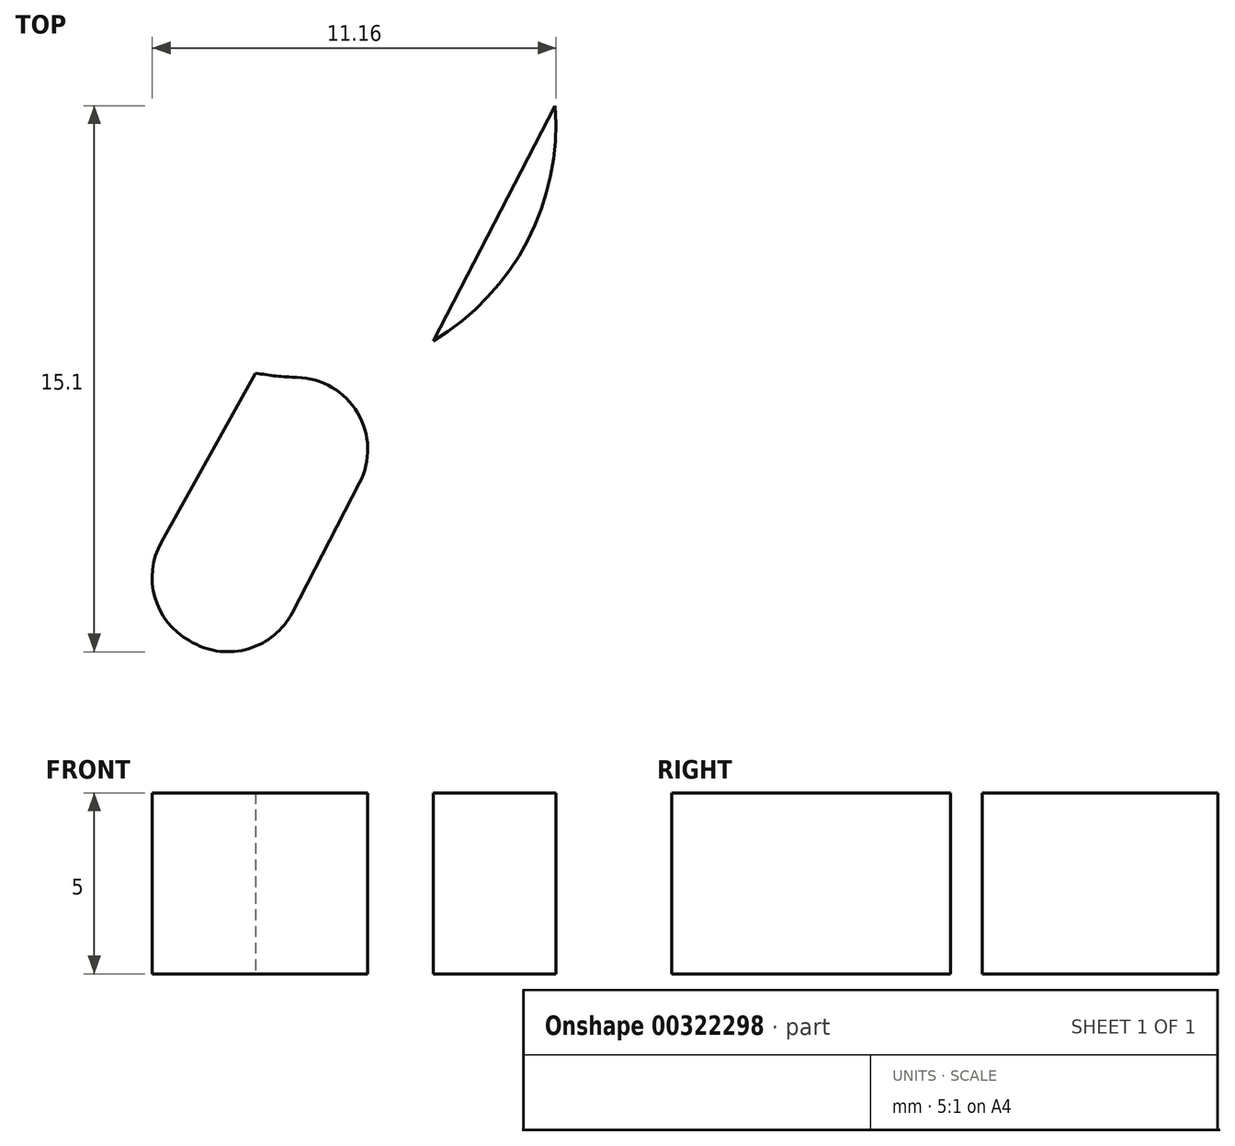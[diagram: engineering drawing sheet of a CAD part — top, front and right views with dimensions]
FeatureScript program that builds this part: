
annotation { "Feature Type Name" : "Feature", "Feature Type Description" : "" }
export const myFeature = defineFeature(function(context is Context, id is Id, definition is map)
    precondition{}
    {
        {
            var Q0;
            Q0=qCreatedBy(makeId("Top.planeOp"),FACE);
            var sketch = newSketch(context, id + "F0", { "sketchPlane" : qUnion([Q0])});
            skCircle(sketch, "E0", {"center": v(0, 0) * mm, "radius": 10 * mm, "construction": true});
            skArc(sketch, "E1", {"start": v(-8.14, 12.6) * mm, "mid": v(7.17, 13.17) * mm, "end": v(15, 0) * mm});
            skArc(sketch, "E2.0", {"start": v(-14.53, 20.34) * mm, "mid": v(14.2, 20.58) * mm, "end": v(24.18, -6.35) * mm});
            skLineSegment(sketch, "E3", {"start": v(15, 0) * mm, "end": v(15, 0) * mm});
            skLineSegment(sketch, "E4", {"start": v(-8.14, 12.6) * mm, "end": v(-14.53, 20.34) * mm});
            skLineSegment(sketch, "E5", {"start": v(15, 0) * mm, "end": v(-4.3, -37.44) * mm});
            skLineSegment(sketch, "E6", {"start": v(-1.24, -55.34) * mm, "end": v(24.18, -6.35) * mm});
            skLineSegment(sketch, "E7", {"start": v(0, -40) * mm, "end": v(17.35, -6.35) * mm, "construction": true});
            skCircle(sketch, "E8", {"center": v(13.03, -14.72) * mm, "radius": 0.5 * mm});
            skCircle(sketch, "E9", {"center": v(15.86, -9.24) * mm, "radius": 0.5 * mm});
            skCircle(sketch, "E10", {"center": v(4.12, -32) * mm, "radius": 0.5 * mm});
            skLineSegment(sketch, "E11", {"start": v(24.18, -6.35) * mm, "end": v(15, 0) * mm, "construction": true});
            skCircle(sketch, "E12", {"center": v(0, -40) * mm, "radius": 1.25 * mm});
            skLineSegment(sketch, "E13", {"start": v(-1.24, -55.34) * mm, "end": v(-4.88, -53.3) * mm});
            skLineSegment(sketch, "E14", {"start": v(-4.88, -53.3) * mm, "end": v(-0.98, -46.3) * mm});
            skCircle(sketch, "E15", {"center": v(0, -40) * mm, "radius": 3.5 * mm, "construction": true});
            skArc(sketch, "E16", {"start": v(-2.2, -33.35) * mm, "mid": v(-3.9, -45.82) * mm, "end": v(6.98, -39.5) * mm});
            skCircle(sketch, "E17", {"center": v(0, -40) * mm, "radius": 7.5 * mm, "construction": true});
            skSolve(sketch);
        }
        {
            var Q0;
            Q0=makeQuery(id+"F0.imprint","IMPRINT",FACE,{"disambiguationData":[TD([[makeQuery(id+"F0.imprint","IMPRINT",EDGE,{"derivedFrom":sQuery(id+"F0.wireOp",EDGE,"Jz9K82jg-m8px-su0A-Sm9u-fOnqXrv2IYMf.bottom")}),-1.0]])]});
            var Q1;
            {var subQ0=sQuery(id+"F0.wireOp",EDGE,"fhU8v1BW-l61l-G27y-Rx19-Y7ilPkFgEnLg");Q1=makeQuery(id+"F0.imprint","IMPRINT",FACE,{"disambiguationData":[TD([[makeQuery(id+"F0.imprint","IMPRINT",EDGE,{"derivedFrom":subQ0}),-1.0]])]});}
            var Q2;
            {var subQ0=sQuery(id+"F0.wireOp",EDGE,"8P200vXd-Ijfn-xAMS-56KQ-ENW5ZjM40npd");Q2=makeQuery(id+"F0.imprint","IMPRINT",FACE,{"disambiguationData":[TD([[makeQuery(id+"F0.imprint","IMPRINT",EDGE,{"derivedFrom":subQ0}),-1.0]])]});}
            var Q3;
            {var subQ0=sQuery(id+"F0.wireOp",EDGE,"orjRLi3t-RLLj-2wEO-kTLT-H2r4xHH4hWms");Q3=makeQuery(id+"F0.imprint","IMPRINT",FACE,{"disambiguationData":[TD([[makeQuery(id+"F0.imprint","IMPRINT",EDGE,{"derivedFrom":subQ0}),1.0]])]});}
            var Q4;
            Q4=makeQuery(id+"F0.imprint","IMPRINT",FACE,{"disambiguationData":[TD([[makeQuery(id+"F0.imprint","IMPRINT",EDGE,{"derivedFrom":sQuery(id+"F0.wireOp",EDGE,"WSkCF9DG-Oxax-l4pN-4FB5-CQ0lKUTtnC4r")}),-1.0]])]});
            var Q5;
            Q5=makeQuery(id+"F0.imprint","IMPRINT",FACE,{"disambiguationData":[TD([[makeQuery(id+"F0.imprint","IMPRINT",EDGE,{"derivedFrom":sQuery(id+"F0.wireOp",EDGE,"E1")}),1.0]])]});
            var Q6;
            {var subQ0=sQuery(id+"F0.wireOp",EDGE,"E13");Q6=makeQuery(id+"F0.imprint","IMPRINT",FACE,{"disambiguationData":[TD([[makeQuery(id+"F0.imprint","IMPRINT",EDGE,{"derivedFrom":subQ0}),-1.0]])]});}
            var Q7;
            {var subQ0=sQuery(id+"F0.wireOp",EDGE,"E16");var subQ1=sQuery(id+"F0.wireOp",EDGE,"E6");var subQ2=makeQuery(id+"F0.imprint","INTERSECT",VERTEX,{"disambiguationData":[OD(0.0)],"derivedFrom":[subQ1,subQ0]});Q7=makeQuery(id+"F0.imprint","IMPRINT",FACE,{"disambiguationData":[TD([[makeQuery(id+"F0.imprint","IMPRINT",EDGE,{"disambiguationData":[TD([[subQ2,1.0]])],"derivedFrom":subQ1}),-1.0]])]});}
            extrude(context, id + "F1", {"entities" : qUnion([Q0, Q1, Q2, Q3, Q4, Q5, Q6, Q7]), "depth" : 5 * mm});
        }
        {
            var Q0;
            Q0=makeQuery(id+"F1.opExtrude","SWEPT_EDGE",EDGE,{"disambiguationData":[OSD([sQuery(id+"F0.wireOp",EDGE,"E6"),sQuery(id+"F0.wireOp",EDGE,"EW70MQ4d-FGGr-7KGx-LwrU-hoHUrzoy7zRc")])]});
            var Q1;
            Q1=makeQuery(id+"F1.opExtrude","SWEPT_EDGE",EDGE,{"disambiguationData":[OSD([sQuery(id+"F0.wireOp",EDGE,"E6"),sQuery(id+"F0.wireOp",EDGE,"67d6aa5d-6902-4030-880d-f36d43311ed0")])]});
            var Q2;
            Q2=makeQuery(id+"F1.opExtrude","SWEPT_EDGE",EDGE,{"disambiguationData":[OSD([sQuery(id+"F0.wireOp",EDGE,"E1"),sQuery(id+"F0.wireOp",EDGE,"E5")])]});
            var Q3;
            Q3=makeQuery(id+"F1.opExtrude","SWEPT_EDGE",EDGE,{"disambiguationData":[OSD([sQuery(id+"F0.wireOp",EDGE,"E5"),sQuery(id+"F0.wireOp",EDGE,"67d6aa5d-6902-4030-880d-f36d43311ed0")])]});
            var Q4;
            Q4=makeQuery(id+"F1.opExtrude","SWEPT_EDGE",EDGE,{"disambiguationData":[OSD([sQuery(id+"F0.wireOp",EDGE,"E1"),sQuery(id+"F0.wireOp",EDGE,"E4")])]});
            var Q5;
            Q5=makeQuery(id+"F1.opExtrude","SWEPT_EDGE",EDGE,{"disambiguationData":[OSD([sQuery(id+"F0.wireOp",EDGE,"E1"),sQuery(id+"F0.wireOp",EDGE,"E5")])]});
            var Q6;
            Q6=makeQuery(id+"F1.opExtrude","SWEPT_EDGE",EDGE,{"disambiguationData":[OSD([sQuery(id+"F0.wireOp",EDGE,"RYZ3omyr-3mdL-A6w5-BGOq-hXHIxv6qc5nw"),sQuery(id+"F0.wireOp",EDGE,"d1fIG5eH-qDmN-3SeZ-uWdY-TunVUHv83kn7")])]});
            var Q7;
            Q7=makeQuery(id+"F1.opExtrude","SWEPT_EDGE",EDGE,{"disambiguationData":[OSD([sQuery(id+"F0.wireOp",EDGE,"WSkCF9DG-Oxax-l4pN-4FB5-CQ0lKUTtnC4r"),sQuery(id+"F0.wireOp",EDGE,"RYZ3omyr-3mdL-A6w5-BGOq-hXHIxv6qc5nw")])]});
            var Q8;
            Q8=makeQuery(id+"F1.opExtrude","SWEPT_EDGE",EDGE,{"disambiguationData":[OSD([sQuery(id+"F0.wireOp",EDGE,"E2.0"),sQuery(id+"F0.wireOp",EDGE,"E4")])]});
            fillet(context, id + "F2", {"entities" : qUnion([Q0, Q1, Q2, Q3, Q4, Q5, Q6, Q7, Q8]), "radius" : 2 * mm, "tangentPropagation" : true, "allowEdgeOverflow" : false});
        }
        {
            var Q0;
            Q0=makeQuery(id+"F1.opExtrude","SWEPT_EDGE",EDGE,{"disambiguationData":[OSD([sQuery(id+"F0.wireOp",EDGE,"E6"),sQuery(id+"F0.wireOp",EDGE,"orjRLi3t-RLLj-2wEO-kTLT-H2r4xHH4hWms")])]});
            var Q1;
            Q1=makeQuery(id+"F1.opExtrude","SWEPT_EDGE",EDGE,{"disambiguationData":[OSD([sQuery(id+"F0.wireOp",EDGE,"WSkCF9DG-Oxax-l4pN-4FB5-CQ0lKUTtnC4r"),sQuery(id+"F0.wireOp",EDGE,"EW70MQ4d-FGGr-7KGx-LwrU-hoHUrzoy7zRc")])]});
            var Q2;
            Q2=makeQuery(id+"F1.opExtrude","SWEPT_EDGE",EDGE,{"disambiguationData":[OSD([sQuery(id+"F0.wireOp",EDGE,"E13"),sQuery(id+"F0.wireOp",EDGE,"E14")])]});
            fillet(context, id + "F3", {"entities" : qUnion([Q0, Q1, Q2]), "radius" : 2 * mm, "tangentPropagation" : true, "allowEdgeOverflow" : false});
        }
    });
